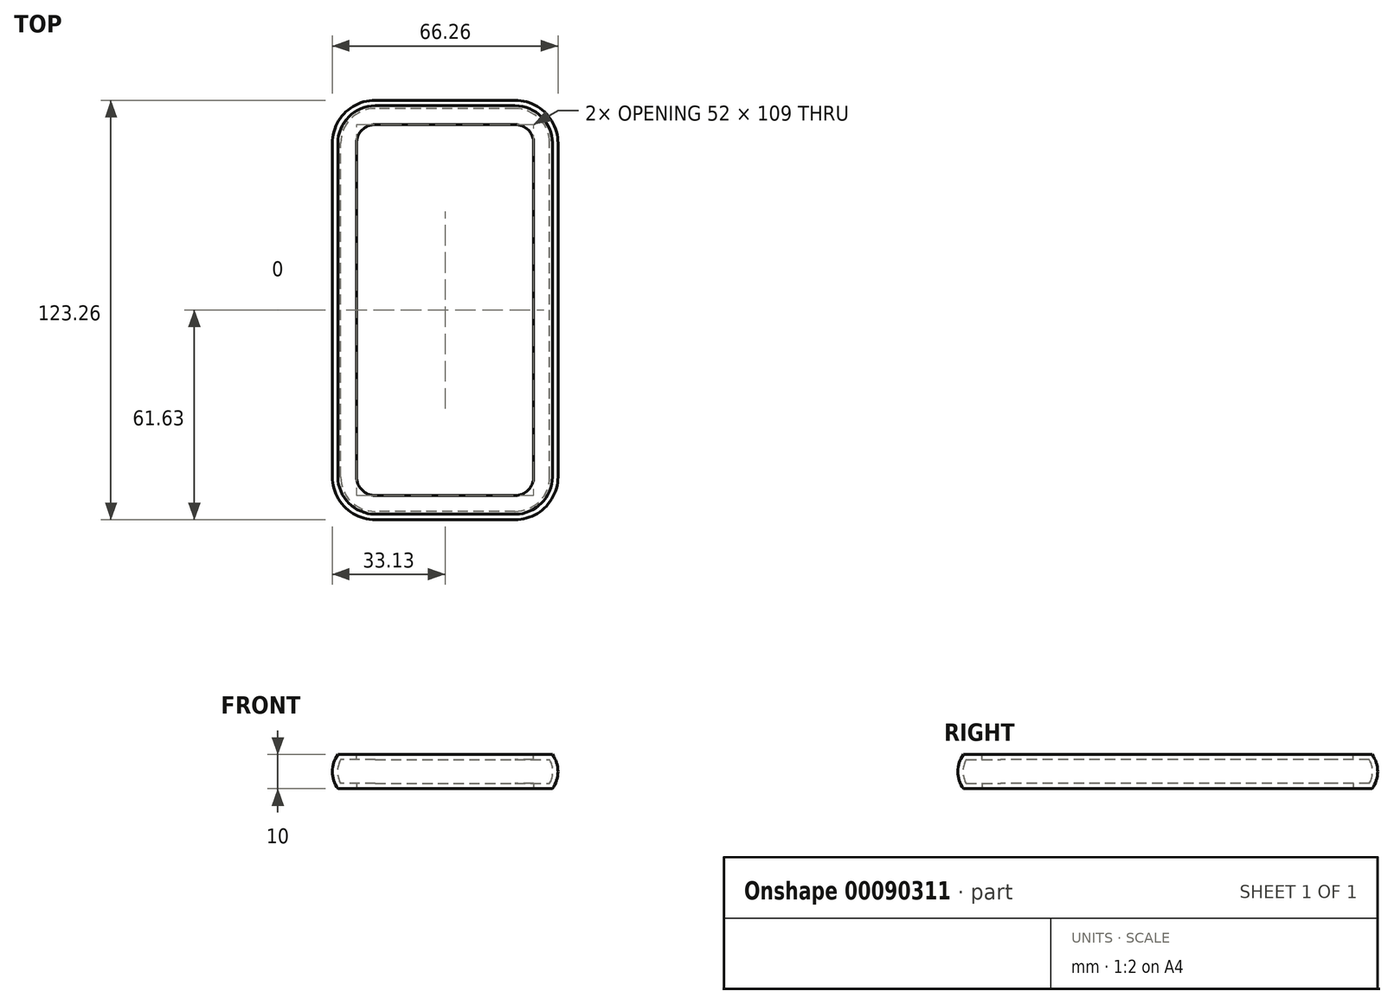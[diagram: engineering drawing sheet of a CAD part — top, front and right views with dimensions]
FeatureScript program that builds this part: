
annotation { "Feature Type Name" : "Feature", "Feature Type Description" : "" }
export const myFeature = defineFeature(function(context is Context, id is Id, definition is map)
    precondition{}
    {
        {
            var Q0;
            Q0=qCreatedBy(makeId("Top.planeOp"),FACE);
            var sketch = newSketch(context, id + "F0", { "sketchPlane" : qUnion([Q0])});
            skLineSegment(sketch, "E0.bottom", {"start": v(-20.5, 58) * mm, "end": v(20.5, 58) * mm});
            skLineSegment(sketch, "E0.top", {"start": v(-20.5, -58) * mm, "end": v(20.5, -58) * mm});
            skLineSegment(sketch, "E0.left", {"start": v(-29.5, 49) * mm, "end": v(-29.5, -49) * mm});
            skLineSegment(sketch, "E0.right", {"start": v(29.5, 49) * mm, "end": v(29.5, -49) * mm});
            skArc(sketch, "E1.filletArc", {"start": v(-20.5, 58) * mm, "mid": v(-26.86, 55.36) * mm, "end": v(-29.5, 49) * mm});
            skArc(sketch, "E2.filletArc", {"start": v(20.5, -58) * mm, "mid": v(26.86, -55.36) * mm, "end": v(29.5, -49) * mm});
            skArc(sketch, "E3.filletArc", {"start": v(-29.5, -49) * mm, "mid": v(-26.86, -55.36) * mm, "end": v(-20.5, -58) * mm});
            skArc(sketch, "E4.filletArc", {"start": v(29.5, 49) * mm, "mid": v(26.86, 55.36) * mm, "end": v(20.5, 58) * mm});
            skArc(sketch, "E5.0", {"start": v(31.5, 49) * mm, "mid": v(28.28, 56.78) * mm, "end": v(20.5, 60) * mm});
            skLineSegment(sketch, "E5.1", {"start": v(31.5, 49) * mm, "end": v(31.5, -49) * mm});
            skLineSegment(sketch, "E5.2", {"start": v(-31.5, 49.91) * mm, "end": v(-31.5, -49) * mm});
            skArc(sketch, "E5.3", {"start": v(-31.5, -49) * mm, "mid": v(-28.28, -56.78) * mm, "end": v(-20.5, -60) * mm});
            skLineSegment(sketch, "E5.4", {"start": v(-20.5, -60) * mm, "end": v(20.5, -60) * mm});
            skArc(sketch, "E5.5", {"start": v(20.5, -60) * mm, "mid": v(28.28, -56.78) * mm, "end": v(31.5, -49) * mm});
            skLineSegment(sketch, "E6.0", {"start": v(-20.5, 60) * mm, "end": v(20.5, 60) * mm});
            skArc(sketch, "E6.1", {"start": v(-20.5, 60) * mm, "mid": v(-28.28, 56.78) * mm, "end": v(-31.5, 49) * mm});
            skArc(sketch, "E7.0", {"start": v(-20.5, 62) * mm, "mid": v(-29.7, 58.2) * mm, "end": v(-33.5, 49) * mm});
            skArc(sketch, "E8.0", {"start": v(33.5, 49) * mm, "mid": v(29.7, 58.2) * mm, "end": v(20.5, 62) * mm});
            skArc(sketch, "E9.0", {"start": v(-33.5, -49) * mm, "mid": v(-29.7, -58.2) * mm, "end": v(-20.5, -62) * mm});
            skArc(sketch, "E10.0", {"start": v(20.5, -62) * mm, "mid": v(29.7, -58.2) * mm, "end": v(33.5, -49) * mm});
            skSolve(sketch);
        }
        {
            var Q0;
            Q0=makeQuery(id+"F0.imprint","IMPRINT",FACE,{"disambiguationData":[TD([[makeQuery(id+"F0.imprint","IMPRINT",EDGE,{"derivedFrom":sQuery(id+"F0.wireOp",EDGE,"E0.bottom")}),1.0]])]});
            extrude(context, id + "F1", {"entities" : qUnion([Q0]), "endBound" : BoundingType.SYMMETRIC, "depth" : 10 * mm});
        }
        {
            var Q0;
            Q0=qCreatedBy(makeId("Front.planeOp"),FACE);
            var sketch = newSketch(context, id + "F2", { "sketchPlane" : qUnion([Q0])});
            skLineSegment(sketch, "E11.0", {"start": v(31.5, 5) * mm, "end": v(31.5, -5) * mm});
            skLineSegment(sketch, "E12.0", {"start": v(-31.5, 5) * mm, "end": v(-31.5, -5) * mm});
            skArc(sketch, "E13", {"start": v(-31.5, 5) * mm, "mid": v(-33.13, 0) * mm, "end": v(-31.5, -5) * mm});
            skArc(sketch, "E14.MirrorCS", {"start": v(31.5, 5) * mm, "mid": v(33.13, 0) * mm, "end": v(31.5, -5) * mm});
            skSolve(sketch);
        }
        {
            var Q0;
            Q0=makeQuery(id+"F2.imprint","IMPRINT",FACE,{"disambiguationData":[TD([[makeQuery(id+"F2.imprint","IMPRINT",EDGE,{"derivedFrom":sQuery(id+"F2.wireOp",EDGE,"E12.0")}),-1.0]])]});
            var Q1;
            Q1=makeQuery(id+"F2.imprint","IMPRINT",FACE,{"disambiguationData":[TD([[makeQuery(id+"F2.imprint","IMPRINT",EDGE,{"derivedFrom":sQuery(id+"F2.wireOp",EDGE,"E11.0")}),1.0]])]});
            extrude(context, id + "F3", {"entities" : qUnion([Q0, Q1]), "operationType" : NewBodyOperationType.ADD, "endBound" : BoundingType.SYMMETRIC, "depth" : 98 * mm});
        }
        {
            var Q0;
            Q0=qCreatedBy(makeId("Right.planeOp"),FACE);
            var sketch = newSketch(context, id + "F4", { "sketchPlane" : qUnion([Q0])});
            skLineSegment(sketch, "E15.0", {"start": v(60, 5) * mm, "end": v(60, -5) * mm});
            skLineSegment(sketch, "E16.0", {"start": v(-60, 5) * mm, "end": v(-60, -5) * mm});
            skArc(sketch, "E17", {"start": v(60, -5) * mm, "mid": v(61.63, 0) * mm, "end": v(60, 5) * mm});
            skArc(sketch, "E18.MirrorCS", {"start": v(-60, -5) * mm, "mid": v(-61.63, 0) * mm, "end": v(-60, 5) * mm});
            skSolve(sketch);
        }
        {
            var Q0;
            Q0 = qSketchRegion(id + "F4", true);
            extrude(context, id + "F5", {"entities" : qUnion([Q0]), "operationType" : NewBodyOperationType.ADD, "endBound" : BoundingType.SYMMETRIC, "depth" : 41 * mm});
        }
        {
            var Q0;
            Q0=makeQuery(id+"F5.opExtrude","CAP_FACE",FACE,{"disambiguationData":[OSD([sQuery(id+"F4.wireOp",EDGE,"E15.0"),sQuery(id+"F4.wireOp",EDGE,"E17")])],"isStart":true});
            var sketch = newSketch(context, id + "F6", { "sketchPlane" : qUnion([Q0])});
            skArc(sketch, "E19.0", {"start": v(-60, -5) * mm, "mid": v(-61.63, 0) * mm, "end": v(-60, 5) * mm});
            skLineSegment(sketch, "E20.0", {"start": v(-60, 5) * mm, "end": v(-60, -5) * mm});
            skSolve(sketch);
        }
        {
            var Q0;
            Q0=makeQuery(id+"F6.imprint","IMPRINT",FACE,{"disambiguationData":[TD([[makeQuery(id+"F6.imprint","IMPRINT",EDGE,{"derivedFrom":sQuery(id+"F6.wireOp",EDGE,"E19.0")}),-1.0]])]});
            var Q1;
            Q1=sQuery(id+"F0.wireOp",EDGE,"E7.0");
            sweep(context, id + "F7", {"operationType" : NewBodyOperationType.ADD, "profiles" : qUnion([Q0]), "path" : qUnion([Q1])});
        }
        {
            var Q0;
            Q0=makeQuery(id+"F5.opExtrude","CAP_FACE",FACE,{"disambiguationData":[OSD([sQuery(id+"F4.wireOp",EDGE,"E15.0"),sQuery(id+"F4.wireOp",EDGE,"E17")])],"isStart":false});
            var sketch = newSketch(context, id + "F8", { "sketchPlane" : qUnion([Q0])});
            skArc(sketch, "E21.0", {"start": v(60, -5) * mm, "mid": v(61.63, 0) * mm, "end": v(60, 5) * mm});
            skLineSegment(sketch, "E22.0", {"start": v(60, 5) * mm, "end": v(60, -5) * mm});
            skSolve(sketch);
        }
        {
            var Q0;
            Q0=makeQuery(id+"F8.imprint","IMPRINT",FACE,{"disambiguationData":[TD([[makeQuery(id+"F8.imprint","IMPRINT",EDGE,{"derivedFrom":sQuery(id+"F8.wireOp",EDGE,"E21.0")}),1.0]])]});
            var Q1;
            Q1=sQuery(id+"F0.wireOp",EDGE,"E8.0");
            sweep(context, id + "F9", {"operationType" : NewBodyOperationType.ADD, "profiles" : qUnion([Q0]), "path" : qUnion([Q1])});
        }
        {
            var Q0;
            Q0=makeQuery(id+"F5.opExtrude","CAP_FACE",FACE,{"disambiguationData":[OSD([sQuery(id+"F4.wireOp",EDGE,"E16.0"),sQuery(id+"F4.wireOp",EDGE,"E18.MirrorCS")])],"isStart":false});
            var sketch = newSketch(context, id + "F10", { "sketchPlane" : qUnion([Q0])});
            skLineSegment(sketch, "E23.0", {"start": v(-60, 5) * mm, "end": v(-60, -5) * mm});
            skArc(sketch, "E24.0", {"start": v(-60, -5) * mm, "mid": v(-61.63, 0) * mm, "end": v(-60, 5) * mm});
            skSolve(sketch);
        }
        {
            var Q0;
            Q0=makeQuery(id+"F10.imprint","IMPRINT",FACE,{"disambiguationData":[TD([[makeQuery(id+"F10.imprint","IMPRINT",EDGE,{"derivedFrom":sQuery(id+"F10.wireOp",EDGE,"E23.0")}),-1.0]])]});
            var Q1;
            Q1=sQuery(id+"F0.wireOp",EDGE,"E10.0");
            sweep(context, id + "F11", {"operationType" : NewBodyOperationType.ADD, "profiles" : qUnion([Q0]), "path" : qUnion([Q1])});
        }
        {
            var Q0;
            Q0=makeQuery(id+"F5.opExtrude","CAP_FACE",FACE,{"disambiguationData":[OSD([sQuery(id+"F4.wireOp",EDGE,"E16.0"),sQuery(id+"F4.wireOp",EDGE,"E18.MirrorCS")])],"isStart":true});
            var sketch = newSketch(context, id + "F12", { "sketchPlane" : qUnion([Q0])});
            skLineSegment(sketch, "E25.0", {"start": v(60, 5) * mm, "end": v(60, -5) * mm});
            skArc(sketch, "E26.0", {"start": v(60, -5) * mm, "mid": v(61.63, 0) * mm, "end": v(60, 5) * mm});
            skSolve(sketch);
        }
        {
            var Q0;
            Q0=makeQuery(id+"F12.imprint","IMPRINT",FACE,{"disambiguationData":[TD([[makeQuery(id+"F12.imprint","IMPRINT",EDGE,{"derivedFrom":sQuery(id+"F12.wireOp",EDGE,"E25.0")}),1.0]])]});
            var Q1;
            Q1=sQuery(id+"F0.wireOp",EDGE,"E9.0");
            sweep(context, id + "F13", {"operationType" : NewBodyOperationType.ADD, "profiles" : qUnion([Q0]), "path" : qUnion([Q1])});
        }
        {
            var Q0;
            Q0=makeQuery(id+"F1.opExtrude","CAP_FACE",FACE,{"disambiguationData":[OSD([sQuery(id+"F0.wireOp",EDGE,"E0.bottom"),sQuery(id+"F0.wireOp",EDGE,"E0.top"),sQuery(id+"F0.wireOp",EDGE,"E0.left"),sQuery(id+"F0.wireOp",EDGE,"E0.right"),sQuery(id+"F0.wireOp",EDGE,"E1.filletArc"),sQuery(id+"F0.wireOp",EDGE,"E2.filletArc"),sQuery(id+"F0.wireOp",EDGE,"E3.filletArc"),sQuery(id+"F0.wireOp",EDGE,"E4.filletArc"),sQuery(id+"F0.wireOp",EDGE,"E5.0"),sQuery(id+"F0.wireOp",EDGE,"E5.1"),sQuery(id+"F0.wireOp",EDGE,"E5.2"),sQuery(id+"F0.wireOp",EDGE,"E5.3"),sQuery(id+"F0.wireOp",EDGE,"E5.4"),sQuery(id+"F0.wireOp",EDGE,"E5.5"),sQuery(id+"F0.wireOp",EDGE,"E6.0"),sQuery(id+"F0.wireOp",EDGE,"E6.1")])],"isStart":false});
            var sketch = newSketch(context, id + "F14", { "sketchPlane" : qUnion([Q0])});
            skArc(sketch, "E27.0", {"start": v(-20.5, 60) * mm, "mid": v(-28.28, 56.78) * mm, "end": v(-31.5, 49) * mm});
            skLineSegment(sketch, "E28.0", {"start": v(-31.5, 49) * mm, "end": v(-31.5, -49) * mm});
            skArc(sketch, "E29.0", {"start": v(-31.5, -49) * mm, "mid": v(-28.28, -56.78) * mm, "end": v(-20.5, -60) * mm});
            skLineSegment(sketch, "E30.0", {"start": v(-20.5, -60) * mm, "end": v(20.5, -60) * mm});
            skArc(sketch, "E31.0", {"start": v(20.5, -60) * mm, "mid": v(28.28, -56.78) * mm, "end": v(31.5, -49) * mm});
            skLineSegment(sketch, "E32.0", {"start": v(31.5, 49) * mm, "end": v(31.5, -49) * mm});
            skArc(sketch, "E33.0", {"start": v(31.5, 49) * mm, "mid": v(28.28, 56.78) * mm, "end": v(20.5, 60) * mm});
            skLineSegment(sketch, "E34.0", {"start": v(-20.5, 60) * mm, "end": v(20.5, 60) * mm});
            skArc(sketch, "E35.0", {"start": v(-20.5, 54.5) * mm, "mid": v(-24.39, 52.89) * mm, "end": v(-26, 49) * mm});
            skLineSegment(sketch, "E35.1", {"start": v(-26, 49) * mm, "end": v(-26, -49) * mm});
            skLineSegment(sketch, "E35.2", {"start": v(-20.5, 54.5) * mm, "end": v(20.5, 54.5) * mm});
            skArc(sketch, "E35.3", {"start": v(-26, -49) * mm, "mid": v(-24.39, -52.89) * mm, "end": v(-20.5, -54.5) * mm});
            skArc(sketch, "E35.4", {"start": v(26, 49) * mm, "mid": v(24.39, 52.89) * mm, "end": v(20.5, 54.5) * mm});
            skLineSegment(sketch, "E35.5", {"start": v(26, 49) * mm, "end": v(26, -49) * mm});
            skArc(sketch, "E35.6", {"start": v(20.5, -54.5) * mm, "mid": v(24.39, -52.89) * mm, "end": v(26, -49) * mm});
            skLineSegment(sketch, "E35.7", {"start": v(-20.5, -54.5) * mm, "end": v(20.5, -54.5) * mm});
            skSolve(sketch);
        }
        {
            var Q0;
            Q0=makeQuery(id+"F14.imprint","IMPRINT",FACE,{"disambiguationData":[TD([[makeQuery(id+"F14.imprint","IMPRINT",EDGE,{"derivedFrom":sQuery(id+"F14.wireOp",EDGE,"E35.0")}),-1.0]])]});
            var Q1;
            Q1=makeQuery(id+"F14.imprint","IMPRINT",FACE,{"disambiguationData":[TD([[makeQuery(id+"F14.imprint","IMPRINT",EDGE,{"derivedFrom":sQuery(id+"F14.wireOp",EDGE,"E27.0")}),1.0]])]});
            extrude(context, id + "F15", {"entities" : qUnion([Q0, Q1]), "oppositeDirection" : true, "depth" : 1.5 * mm});
        }
        {
            var Q0;
            Q0=makeQuery(id+"F15.opExtrude","SWEPT_BODY",BODY,{"disambiguationData":[OSD([sQuery(id+"F14.wireOp",EDGE,"E27.0"),sQuery(id+"F14.wireOp",EDGE,"E28.0"),sQuery(id+"F14.wireOp",EDGE,"E29.0"),sQuery(id+"F14.wireOp",EDGE,"E30.0"),sQuery(id+"F14.wireOp",EDGE,"E31.0"),sQuery(id+"F14.wireOp",EDGE,"E32.0"),sQuery(id+"F14.wireOp",EDGE,"E33.0"),sQuery(id+"F14.wireOp",EDGE,"E34.0"),sQuery(id+"F14.wireOp",EDGE,"E35.0"),sQuery(id+"F14.wireOp",EDGE,"E35.1"),sQuery(id+"F14.wireOp",EDGE,"E35.2"),sQuery(id+"F14.wireOp",EDGE,"E35.3"),sQuery(id+"F14.wireOp",EDGE,"E35.4"),sQuery(id+"F14.wireOp",EDGE,"E35.5"),sQuery(id+"F14.wireOp",EDGE,"E35.6"),sQuery(id+"F14.wireOp",EDGE,"E35.7")])]});
            var Q1;
            Q1=qCreatedBy(makeId("Top.planeOp"),FACE);
            mirror(context, id + "F16", {"operationType" : NewBodyOperationType.ADD, "entities" : qUnion([Q0]), "mirrorPlane" : qUnion([Q1])});
        }
        {
            var Q0;
            Q0=makeQuery(id+"F1.opExtrude","SWEPT_FACE",FACE,{"disambiguationData":[OSD([sQuery(id+"F0.wireOp",EDGE,"E0.right")])]});
            var Q1;
            Q1=makeQuery(id+"F1.opExtrude","SWEPT_FACE",FACE,{"disambiguationData":[OSD([sQuery(id+"F0.wireOp",EDGE,"E2.filletArc")])]});
            var Q2;
            Q2=makeQuery(id+"F1.opExtrude","SWEPT_FACE",FACE,{"disambiguationData":[OSD([sQuery(id+"F0.wireOp",EDGE,"E0.top")])]});
            var Q3;
            Q3=makeQuery(id+"F1.opExtrude","SWEPT_FACE",FACE,{"disambiguationData":[OSD([sQuery(id+"F0.wireOp",EDGE,"E3.filletArc")])]});
            var Q4;
            Q4=makeQuery(id+"F1.opExtrude","SWEPT_FACE",FACE,{"disambiguationData":[OSD([sQuery(id+"F0.wireOp",EDGE,"E0.left")])]});
            var Q5;
            Q5=makeQuery(id+"F1.opExtrude","SWEPT_FACE",FACE,{"disambiguationData":[OSD([sQuery(id+"F0.wireOp",EDGE,"E0.bottom")])]});
            var Q6;
            Q6=makeQuery(id+"F1.opExtrude","SWEPT_FACE",FACE,{"disambiguationData":[OSD([sQuery(id+"F0.wireOp",EDGE,"E4.filletArc")])]});
            var Q7;
            Q7=makeQuery(id+"F1.opExtrude","SWEPT_FACE",FACE,{"disambiguationData":[OSD([sQuery(id+"F0.wireOp",EDGE,"E1.filletArc")])]});
            shell(context, id + "F17", {"entities" : qUnion([Q0, Q1, Q2, Q3, Q4, Q5, Q6, Q7]), "thickness" : 1.5 * mm});
        }
    });
